FCSTD DOCUMENT  (FreeCAD 0.18R16117 (Git))
Label: virtualbed
License: All rights reserved
LicenseURL: http://en.wikipedia.org/wiki/All_rights_reserved
objects: Sketcher::SketchObject×1, PartDesign::Body×1
note: 2 computed .brp shape members not serialized (recipe doc carries the construction recipe); baked Part::Feature solids carry a one-line shape summary decoded from their .brp

FEATURE [Sketcher::SketchObject] Sketch
  MapMode = 2
  Support = -> [XY_Plane]
  sketch-geometry (93):
    g0: LineSegment [constr] StartX=-50 StartY=50 StartZ=0 EndX=50 EndY=50 EndZ=0
    g1: LineSegment [constr] StartX=50 StartY=50 StartZ=0 EndX=50 EndY=-50 EndZ=0
    g2: LineSegment [constr] StartX=50 StartY=-50 StartZ=0 EndX=-50 EndY=-50 EndZ=0
    g3: LineSegment [constr] StartX=-50 StartY=-50 StartZ=0 EndX=-50 EndY=50 EndZ=0
    g4: ArcOfCircle CenterX=-1.04214 CenterY=31.0518 CenterZ=0 NormalX=0 NormalY=0 NormalZ=1 AngleXU=0 Radius=12 StartAngle=5.56633 EndAngle=9.60265
    g5: ArcOfCircle CenterX=-39.37 CenterY=-39.6681 CenterZ=0 NormalX=0 NormalY=0 NormalZ=1 AngleXU=0 Radius=5 StartAngle=2.25514 EndAngle=5.4052
    g6: ArcOfCircle CenterX=-45.332 CenterY=32.1157 CenterZ=0 NormalX=0 NormalY=0 NormalZ=1 AngleXU=0 Radius=3 StartAngle=5.90631 EndAngle=9.92769
    g7: ArcOfCircle CenterX=-37.1114 CenterY=38.7142 CenterZ=0 NormalX=0 NormalY=0 NormalZ=1 AngleXU=0 Radius=3 StartAngle=5.76083 EndAngle=9.94289
    g8: ArcOfCircle CenterX=-28.2365 CenterY=35.991 CenterZ=0 NormalX=0 NormalY=0 NormalZ=1 AngleXU=0 Radius=3 StartAngle=5.3516 EndAngle=9.75743
    g9: ArcOfCircle CenterX=22.1726 CenterY=26.7469 CenterZ=0 NormalX=0 NormalY=0 NormalZ=1 AngleXU=0 Radius=3 StartAngle=0.834516 EndAngle=4.24297
    g10: ArcOfCircle CenterX=35.9134 CenterY=21.1705 CenterZ=0 NormalX=0 NormalY=0 NormalZ=1 AngleXU=0 Radius=3 StartAngle=5.67961 EndAngle=9.47564
    g11: ArcOfCircle CenterX=32.7486 CenterY=32.3751 CenterZ=0 NormalX=0 NormalY=0 NormalZ=1 AngleXU=0 Radius=3 StartAngle=4.8802 EndAngle=9.42967
    g12: LineSegment StartX=-36.1765 StartY=-43.5154 StartZ=0 EndX=2.2969 EndY=-17.9712 EndZ=0
    g13: LineSegment StartX=2.2969 StartY=-17.9712 StartZ=0 EndX=6.2568 EndY=-2.58987 EndZ=0
    g14: LineSegment StartX=6.2568 StartY=-2.58987 StartZ=0 EndX=3.97269 EndY=1.50363 EndZ=0
    g15: LineSegment StartX=3.97269 StartY=1.50363 StartZ=0 EndX=3.47878 EndY=2.49146 EndZ=0
    g16: LineSegment StartX=3.47878 StartY=2.49146 StartZ=0 EndX=2.70262 EndY=3.76153 EndZ=0
    g17: LineSegment StartX=2.70262 StartY=3.76153 StartZ=0 EndX=11.8754 EndY=6.4428 EndZ=0
    g18: LineSegment StartX=11.8754 StartY=6.4428 StartZ=0 EndX=15.2216 EndY=8.48348 EndZ=0
    g19: LineSegment StartX=15.2216 StartY=8.48348 StartZ=0 EndX=37.587 EndY=17.6822 EndZ=0
    g20: LineSegment StartX=37.587 StartY=17.6822 StartZ=0 EndX=38.3833 EndY=19.4678 EndZ=0
    g21: LineSegment StartX=-42.5308 StartY=-35.7939 StartZ=0 EndX=-38.1514 EndY=-25.1679 EndZ=0
    g22: LineSegment StartX=-38.1514 StartY=-25.1679 StartZ=0 EndX=-35.0468 EndY=-18.3942 EndZ=0
    g23: LineSegment StartX=-35.0468 StartY=-18.3942 StartZ=0 EndX=-35.0468 EndY=-13.9489 EndZ=0
    g24: LineSegment StartX=-35.0468 StartY=-13.9489 StartZ=0 EndX=-38.1514 EndY=-8.72753 EndZ=0
    g25: LineSegment StartX=-38.1514 StartY=-8.72753 StartZ=0 EndX=-38.7159 EndY=-2.6594 EndZ=0
    g26: LineSegment StartX=-38.7159 StartY=-2.6594 StartZ=0 EndX=-43.8668 EndY=4.04377 EndZ=0
    g27: LineSegment StartX=-43.8668 StartY=4.04377 StartZ=0 EndX=-46.4199 EndY=14.3051 EndZ=0
    g28: LineSegment StartX=-46.4199 StartY=14.3051 StartZ=0 EndX=-46.4802 EndY=22.42 EndZ=0
    g29: LineSegment StartX=-46.4797 StartY=22.4194 StartZ=0 EndX=-47.9605 EndY=30.6698 EndZ=0
    g30: LineSegment StartX=-42.5425 StartY=31.0117 StartZ=0 EndX=-42.1465 EndY=29.1008 EndZ=0
    g31: LineSegment StartX=-42.1465 StartY=29.1008 StartZ=0 EndX=-41.4888 EndY=28.1359 EndZ=0
    g32: LineSegment StartX=-41.4888 StartY=28.1359 StartZ=0 EndX=-40.8685 EndY=27.9974 EndZ=0
    g33: LineSegment StartX=-40.8685 StartY=27.9974 StartZ=0 EndX=-40.2182 EndY=28.5373 EndZ=0
    g34: LineSegment StartX=-40.2182 StartY=28.5373 StartZ=0 EndX=-39.7786 EndY=30.2063 EndZ=0
    g35: LineSegment StartX=-39.7786 StartY=30.2063 StartZ=0 EndX=-39.973 EndY=31.0604 EndZ=0
    g36: LineSegment StartX=-39.973 StartY=31.0604 StartZ=0 EndX=-40.8735 EndY=32.9896 EndZ=0
    g37: LineSegment StartX=-40.8735 StartY=32.9896 StartZ=0 EndX=-40.7995 EndY=34.4037 EndZ=0
    g38: LineSegment StartX=-40.7995 StartY=34.4037 StartZ=0 EndX=-40.5673 EndY=35.5491 EndZ=0
    g39: LineSegment StartX=-40.5673 StartY=35.5491 StartZ=0 EndX=-40.2394 EndY=36.4651 EndZ=0
    g40: LineSegment StartX=-40.2394 StartY=36.4651 StartZ=0 EndX=-39.7177 EndY=37.2285 EndZ=0
    g41: LineSegment StartX=-34.5114 StartY=37.2174 StartZ=0 EndX=-35.6783 EndY=32.8405 EndZ=0
    g42: LineSegment StartX=-35.6783 StartY=32.8405 StartZ=0 EndX=-34.5818 EndY=32.6381 EndZ=0
    g43: LineSegment StartX=-34.5818 StartY=32.6381 StartZ=0 EndX=-34.1175 EndY=31.9342 EndZ=0
    g44: LineSegment StartX=-34.1175 StartY=31.9342 StartZ=0 EndX=-34.5011 EndY=30.7447 EndZ=0
    g45: LineSegment StartX=-34.5011 StartY=30.7447 StartZ=0 EndX=-35.3098 EndY=29.6235 EndZ=0
    g46: LineSegment StartX=-35.3098 StartY=29.6235 StartZ=0 EndX=-35.2332 EndY=29.0607 EndZ=0
    g47: LineSegment StartX=-35.2332 StartY=29.0607 StartZ=0 EndX=-34.6354 EndY=28.3301 EndZ=0
    g48: LineSegment StartX=-34.6354 StartY=28.3301 StartZ=0 EndX=-33.1176 EndY=28.8286 EndZ=0
    g49: LineSegment StartX=-33.1176 StartY=28.8286 StartZ=0 EndX=-32.6077 EndY=29.5155 EndZ=0
    g50: LineSegment StartX=-32.6077 StartY=29.5155 StartZ=0 EndX=-32.3946 EndY=30.708 EndZ=0
    g51: LineSegment StartX=-32.3946 StartY=30.708 StartZ=0 EndX=-31.5848 EndY=31.9024 EndZ=0
    g52: LineSegment StartX=-31.5848 StartY=31.9024 StartZ=0 EndX=-31.805 EndY=33.432 EndZ=0
    g53: LineSegment StartX=-31.805 StartY=33.432 StartZ=0 EndX=-31.072 EndY=35.0113 EndZ=0
    g54: LineSegment StartX=-26.4468 StartY=33.5833 StartZ=0 EndX=-27.0086 EndY=30.6381 EndZ=0
    g55: LineSegment StartX=-27.0086 StartY=30.6381 StartZ=0 EndX=-25.6636 EndY=29.394 EndZ=0
    g56: LineSegment StartX=-25.6636 StartY=29.394 StartZ=0 EndX=-27.0714 EndY=28.1246 EndZ=0
    g57: LineSegment StartX=-27.0714 StartY=28.1246 StartZ=0 EndX=-28.3337 EndY=27.6095 EndZ=0
    g58: LineSegment StartX=-28.3337 StartY=27.6095 StartZ=0 EndX=-28.5412 EndY=26.1119 EndZ=0
    g59: LineSegment StartX=-28.5412 StartY=26.1119 StartZ=0 EndX=-25.6182 EndY=22.2573 EndZ=0
    g60: LineSegment StartX=-25.6182 StartY=22.2573 StartZ=0 EndX=-23.5032 EndY=21.2456 EndZ=0
    g61: LineSegment StartX=-23.5032 StartY=21.2456 StartZ=0 EndX=-21.1862 EndY=21.1255 EndZ=0
    g62: LineSegment StartX=-21.1862 StartY=21.1255 StartZ=0 EndX=-19.7614 EndY=21.9063 EndZ=0
    g63: LineSegment StartX=-19.7614 StartY=21.9063 StartZ=0 EndX=-18.5459 EndY=24.215 EndZ=0
    g64: LineSegment StartX=-18.5459 StartY=24.215 StartZ=0 EndX=-17.5025 EndY=25.5386 EndZ=0
    g65: LineSegment StartX=-17.5025 StartY=25.5386 StartZ=0 EndX=-14.2532 EndY=26.6508 EndZ=0
    g66: LineSegment StartX=-14.2532 StartY=26.6508 StartZ=0 EndX=-12.6261 EndY=28.0284 EndZ=0
    g67: LineSegment StartX=-12.6261 StartY=28.0284 StartZ=0 EndX=-12.8528 EndY=28.9285 EndZ=0
    g68: LineSegment StartX=8.00433 StartY=23.1675 StartZ=0 EndX=8.04923 EndY=16.583 EndZ=0
    g69: LineSegment StartX=8.04923 StartY=16.583 StartZ=0 EndX=9.32896 EndY=15.1113 EndZ=0
    g70: LineSegment StartX=9.32896 StartY=15.1113 StartZ=0 EndX=11.3643 EndY=15.9712 EndZ=0
    g71: LineSegment StartX=11.3643 StartY=15.9712 StartZ=0 EndX=13.3428 EndY=17.9926 EndZ=0
    g72: LineSegment StartX=13.3428 StartY=17.9926 StartZ=0 EndX=13.7777 EndY=19.3248 EndZ=0
    g73: LineSegment StartX=13.7777 StartY=19.3248 StartZ=0 EndX=14.6085 EndY=20.048 EndZ=0
    g74: LineSegment StartX=14.6085 StartY=20.048 StartZ=0 EndX=16.9935 EndY=20.1209 EndZ=0
    g75: LineSegment StartX=16.9935 StartY=20.1209 StartZ=0 EndX=20.3983 EndY=19.3758 EndZ=0
    g76: LineSegment StartX=20.3983 StartY=19.3758 StartZ=0 EndX=21.4732 EndY=18.7157 EndZ=0
    g77: LineSegment StartX=21.4732 StartY=18.7157 StartZ=0 EndX=22.968 EndY=19.0801 EndZ=0
    g78: LineSegment StartX=22.968 StartY=19.0801 StartZ=0 EndX=23.7013 EndY=19.9288 EndZ=0
    g79: LineSegment StartX=23.7013 StartY=19.9288 StartZ=0 EndX=24.2102 EndY=21.0428 EndZ=0
    g80: LineSegment StartX=24.2102 StartY=21.0428 StartZ=0 EndX=23.8033 EndY=22.1735 EndZ=0
    g81: LineSegment StartX=23.8033 StartY=22.1735 StartZ=0 EndX=22.7755 EndY=22.2784 EndZ=0
    g82: LineSegment StartX=22.7755 StartY=22.2784 StartZ=0 EndX=20.8155 EndY=24.0714 EndZ=0
    g83: LineSegment StartX=24.1872 StartY=28.9698 StartZ=0 EndX=26.5388 EndY=25.3223 EndZ=0
    g84: LineSegment StartX=26.5388 StartY=25.3223 StartZ=0 EndX=28.8106 EndY=26.8311 EndZ=0
    g85: LineSegment StartX=28.8106 StartY=26.8311 StartZ=0 EndX=29.7486 EndY=32.3604 EndZ=0
    g86: LineSegment StartX=33.2497 StartY=29.4172 StartZ=0 EndX=33.154 EndY=25.2507 EndZ=0
    g87: LineSegment StartX=33.154 StartY=25.2507 StartZ=0 EndX=30.4831 EndY=23.4819 EndZ=0
    g88: LineSegment StartX=30.4831 StartY=23.4819 StartZ=0 EndX=29.6297 EndY=19.6578 EndZ=0
    g89: LineSegment StartX=29.6297 StartY=19.6578 StartZ=0 EndX=30.7586 EndY=19.0277 EndZ=0
    g90: LineSegment StartX=30.7586 StartY=19.0277 StartZ=0 EndX=32.9173 EndY=21.018 EndZ=0
    g91: LineSegment StartX=-36.1765 StartY=-43.5154 StartZ=0 EndX=-36.1765 EndY=-43.5154 EndZ=0
    g92: GeomPoint X=-36.1765 Y=-43.5154 Z=0
  constraints (98):
    c: Coincident(g0,g1)
    c: Coincident(g1,g2)
    c: Coincident(g2,g3)
    c: Coincident(g3,g0)
    c: Horizontal(g2)
    c: Vertical(g3)
    c: DistanceX(g0,g0) = 100
    c: DistanceY(g1,g1) = 100
    c: Symmetric(g1,g0,g-1)
    c: Symmetric(g0,g0,g-2)
    c: Radius(g4) = 12
    c: Radius(g5) = 5
    c: Radius(g6) = 3
    c: Equal(g6, g7-g11) x5
    c: Coincident(g12,g13)
    c: Coincident(g13,g14)
    c: Coincident(g14,g15)
    c: Coincident(g15,g16)
    c: Coincident(g16,g17)
    c: Coincident(g17,g18)
    c: Coincident(g18,g19)
    c: Coincident(g19,g20)
    c: Coincident(g21,g22)
    c: Coincident(g22,g23)
    c: Coincident(g23,g24)
    c: Coincident(g24,g25)
    c: Coincident(g25,g26)
    c: Coincident(g26,g27)
    c: Coincident(g27,g28)
    c: Coincident(g30,g31)
    c: Coincident(g31,g32)
    c: Coincident(g32,g33)
    c: Coincident(g33,g34)
    c: Coincident(g34,g35)
    c: Coincident(g35,g36)
    c: Coincident(g36,g37)
    c: Coincident(g37,g38)
    c: Coincident(g38,g39)
    c: Coincident(g39,g40)
    c: Coincident(g41,g42)
    c: Coincident(g42,g43)
    c: Coincident(g43,g44)
    c: Coincident(g44,g45)
    c: Coincident(g45,g46)
    c: Coincident(g46,g47)
    c: Coincident(g47,g48)
    c: Coincident(g48,g49)
    c: Coincident(g49,g50)
    c: Coincident(g50,g51)
    c: Coincident(g51,g52)
    c: Coincident(g52,g53)
    c: Coincident(g54,g55)
    c: Coincident(g55,g56)
    c: Coincident(g56,g57)
    c: Coincident(g57,g58)
    c: Coincident(g58,g59)
    c: Coincident(g59,g60)
    c: Coincident(g60,g61)
    c: Coincident(g61,g62)
    c: Coincident(g62,g63)
    c: Coincident(g63,g64)
    c: Coincident(g64,g65)
    c: Coincident(g65,g66)
    c: Coincident(g66,g67)
    c: Coincident(g68,g69)
    c: Coincident(g69,g70)
    c: Coincident(g70,g71)
    c: Coincident(g71,g72)
    c: Coincident(g72,g73)
    c: Coincident(g73,g74)
    c: Coincident(g74,g75)
    c: Coincident(g75,g76)
    c: Coincident(g76,g77)
    c: Coincident(g77,g78)
    c: Coincident(g78,g79)
    c: Coincident(g79,g80)
    c: Coincident(g80,g81)
    c: Coincident(g81,g82)
    c: Coincident(g83,g84)
    c: Coincident(g86,g87)
    c: Coincident(g87,g88)
    c: Coincident(g88,g89)
    c: Coincident(g89,g90)
    c: Coincident(g9,g82)
    c: Coincident(g10,g20)
    c: Coincident(g10,g90)
    c: Coincident(g11,g85)
    c: Coincident(g8,g53)
    c: Coincident(g7,g40)
    c: Coincident(g6,g29)
    c: Coincident(g4,g67)
    c: Coincident(g5,g21)
    c: Coincident(g6,g30)
    c: Coincident(g7,g41)
    c: Coincident(g8,g54)
    c: Coincident(g68,g4)
    c: Coincident(g9,g83)
    c: Coincident(g86,g11)
FEATURE [PartDesign::Body] Body
  Group = -> [Sketch]
  Origin = -> Origin
